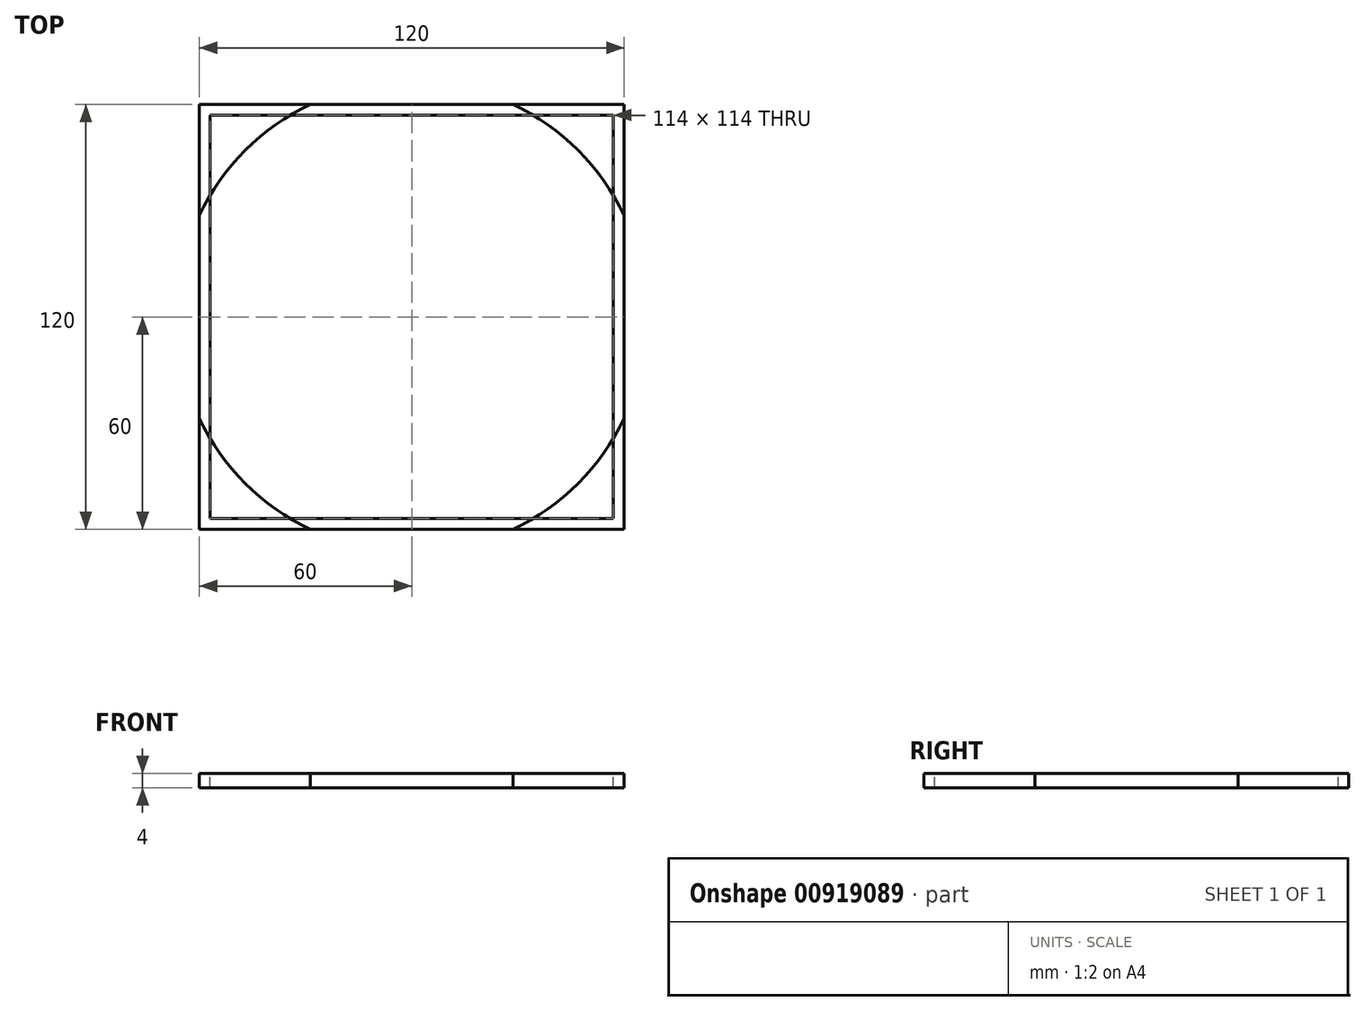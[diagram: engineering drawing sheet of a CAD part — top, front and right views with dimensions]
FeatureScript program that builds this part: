
annotation { "Feature Type Name" : "Feature", "Feature Type Description" : "" }
export const myFeature = defineFeature(function(context is Context, id is Id, definition is map)
    precondition{}
    {
        {
            var Q0;
            Q0=qCreatedBy(makeId("Top.planeOp"),FACE);
            var sketch = newSketch(context, id + "F0", { "sketchPlane" : qUnion([Q0])});
            skLineSegment(sketch, "E0.bottom", {"start": v(-60, 60) * mm, "end": v(60, 60) * mm});
            skLineSegment(sketch, "E0.top", {"start": v(-60, -60) * mm, "end": v(60, -60) * mm});
            skLineSegment(sketch, "E0.left", {"start": v(-60, 60) * mm, "end": v(-60, -60) * mm});
            skLineSegment(sketch, "E0.right", {"start": v(60, 60) * mm, "end": v(60, -60) * mm});
            skSolve(sketch);
        }
        {
            var Q0;
            Q0 = qSketchRegion(id + "F0", true);
            extrude(context, id + "F1", {"entities" : qUnion([Q0]), "depth" : 4 * mm, "offsetDistance" : 25 * mm});
        }
        {
            var Q0;
            Q0=makeQuery(id+"F1.opExtrude","CAP_FACE",FACE,{"disambiguationData":[OSD([sQuery(id+"F0.wireOp",EDGE,"E0.bottom"),sQuery(id+"F0.wireOp",EDGE,"E0.top"),sQuery(id+"F0.wireOp",EDGE,"E0.left"),sQuery(id+"F0.wireOp",EDGE,"E0.right")])],"isStart":false});
            var sketch = newSketch(context, id + "F2", { "sketchPlane" : qUnion([Q0])});
            skCircle(sketch, "E1", {"center": v(0, 0) * mm, "radius": 66.5 * mm});
            skSolve(sketch);
        }
        {
            var Q0;
            {var subQ0=sQuery(id+"F2.wireOp",EDGE,"E1");var subQ8=makeQuery(id+"F1.opExtrude","CAP_EDGE",EDGE,{"disambiguationData":[OSD([sQuery(id+"F0.wireOp",EDGE,"E0.bottom")])],"isStart":false});var subQ11=makeQuery(id+"F2.imprint","INTERSECT",VERTEX,{"disambiguationData":[OD(0.0)],"derivedFrom":[subQ8,subQ0]});Q0=makeQuery(id+"F2.imprint","IMPRINT",FACE,{"disambiguationData":[TD([[makeQuery(id+"F2.imprint","IMPRINT",EDGE,{"disambiguationData":[TD([[subQ11,1.0]])],"derivedFrom":subQ0}),1.0]])]});}
            extrude(context, id + "F3", {"entities" : qUnion([Q0]), "operationType" : NewBodyOperationType.REMOVE, "oppositeDirection" : true, "depth" : 25 * mm, "offsetDistance" : 25 * mm});
        }
        {
            var Q0;
            {var subQ0=sQuery(id+"F0.wireOp",EDGE,"E0.bottom");var subQ1=sQuery(id+"F0.wireOp",EDGE,"E0.left");var subQ2=sQuery(id+"F2.wireOp",EDGE,"E1");Q0=makeQuery(id+"F3.boolean.opBoolean","SPLIT",FACE,{"disambiguationData":[TD([makeQuery(id+"F3.opExtrude","SWEPT_FACE",FACE,{"disambiguationData":[OSD([subQ2]),TDD([makeQuery(id+"F2.imprint","IMPRINT",EDGE,{"disambiguationData":[TD([[makeQuery(id+"F2.imprint","INTERSECT",VERTEX,{"disambiguationData":[OD(1.0)],"derivedFrom":[makeQuery(id+"F1.opExtrude","CAP_EDGE",EDGE,{"disambiguationData":[OSD([subQ0])],"isStart":false}),subQ2]}),-1.0]])],"derivedFrom":subQ2})])]})])],"derivedFrom":makeQuery(id+"F1.opExtrude","CAP_FACE",FACE,{"disambiguationData":[OSD([subQ0,sQuery(id+"F0.wireOp",EDGE,"E0.top"),subQ1,sQuery(id+"F0.wireOp",EDGE,"E0.right")])],"isStart":false})});}
            var sketch = newSketch(context, id + "F4", { "sketchPlane" : qUnion([Q0])});
            skLineSegment(sketch, "E2.bottom", {"start": v(-60, 60) * mm, "end": v(60, 60) * mm});
            skLineSegment(sketch, "E2.top", {"start": v(-60, -60) * mm, "end": v(60, -60) * mm});
            skLineSegment(sketch, "E2.left", {"start": v(-60, 60) * mm, "end": v(-60, -60) * mm});
            skLineSegment(sketch, "E2.right", {"start": v(60, 60) * mm, "end": v(60, -60) * mm});
            skLineSegment(sketch, "E3.bottom", {"start": v(-57, 57) * mm, "end": v(57, 57) * mm});
            skLineSegment(sketch, "E3.top", {"start": v(-57, -57) * mm, "end": v(57, -57) * mm});
            skLineSegment(sketch, "E3.left", {"start": v(-57, 57) * mm, "end": v(-57, -57) * mm});
            skLineSegment(sketch, "E3.right", {"start": v(57, 57) * mm, "end": v(57, -57) * mm});
            skSolve(sketch);
        }
        {
            var Q0;
            {var subQ5=sQuery(id+"F4.wireOp",EDGE,"E2.top");Q0=makeQuery(id+"F4.imprint","IMPRINT",FACE,{"disambiguationData":[TD([[makeQuery(id+"F4.imprint","IMPRINT",EDGE,{"derivedFrom":subQ5}),1.0]])]});}
            var Q1;
            {var subQ7=sQuery(id+"F4.wireOp",EDGE,"E2.left");var subQ8=sQuery(id+"F4.wireOp",EDGE,"E2.bottom");var subQ9=makeQuery(id+"F4.imprint","INTERSECT",VERTEX,{"derivedFrom":[subQ8,subQ7]});Q1=makeQuery(id+"F4.imprint","IMPRINT",FACE,{"disambiguationData":[TD([[makeQuery(id+"F4.imprint","IMPRINT",EDGE,{"disambiguationData":[TD([[subQ9,-1.0]])],"derivedFrom":subQ8}),-1.0]])]});}
            extrude(context, id + "F5", {"entities" : qUnion([Q0, Q1]), "oppositeDirection" : true, "depth" : 4 * mm, "offsetDistance" : 25 * mm});
        }
        {
            var Q0;
            {var subQ0=sQuery(id+"F0.wireOp",EDGE,"E0.bottom");var subQ1=sQuery(id+"F0.wireOp",EDGE,"E0.left");var subQ2=sQuery(id+"F2.wireOp",EDGE,"E1");Q0=makeQuery(id+"F3.boolean.opBoolean","SPLIT",FACE,{"disambiguationData":[TD([makeQuery(id+"F3.opExtrude","SWEPT_FACE",FACE,{"disambiguationData":[OSD([subQ2]),TDD([makeQuery(id+"F2.imprint","IMPRINT",EDGE,{"disambiguationData":[TD([[makeQuery(id+"F2.imprint","INTERSECT",VERTEX,{"disambiguationData":[OD(1.0)],"derivedFrom":[makeQuery(id+"F1.opExtrude","CAP_EDGE",EDGE,{"disambiguationData":[OSD([subQ0])],"isStart":false}),subQ2]}),-1.0]])],"derivedFrom":subQ2})])]})])],"derivedFrom":makeQuery(id+"F1.opExtrude","CAP_FACE",FACE,{"disambiguationData":[OSD([subQ0,sQuery(id+"F0.wireOp",EDGE,"E0.top"),subQ1,sQuery(id+"F0.wireOp",EDGE,"E0.right")])],"isStart":false})});}
            cPlane(context, id + "F6", {"entities" : qUnion([Q0]), "cplaneType" : CPlaneType.OFFSET, "offset" : 40 * mm, "width" : 150 * mm, "height" : 150 * mm});
        }
    });
